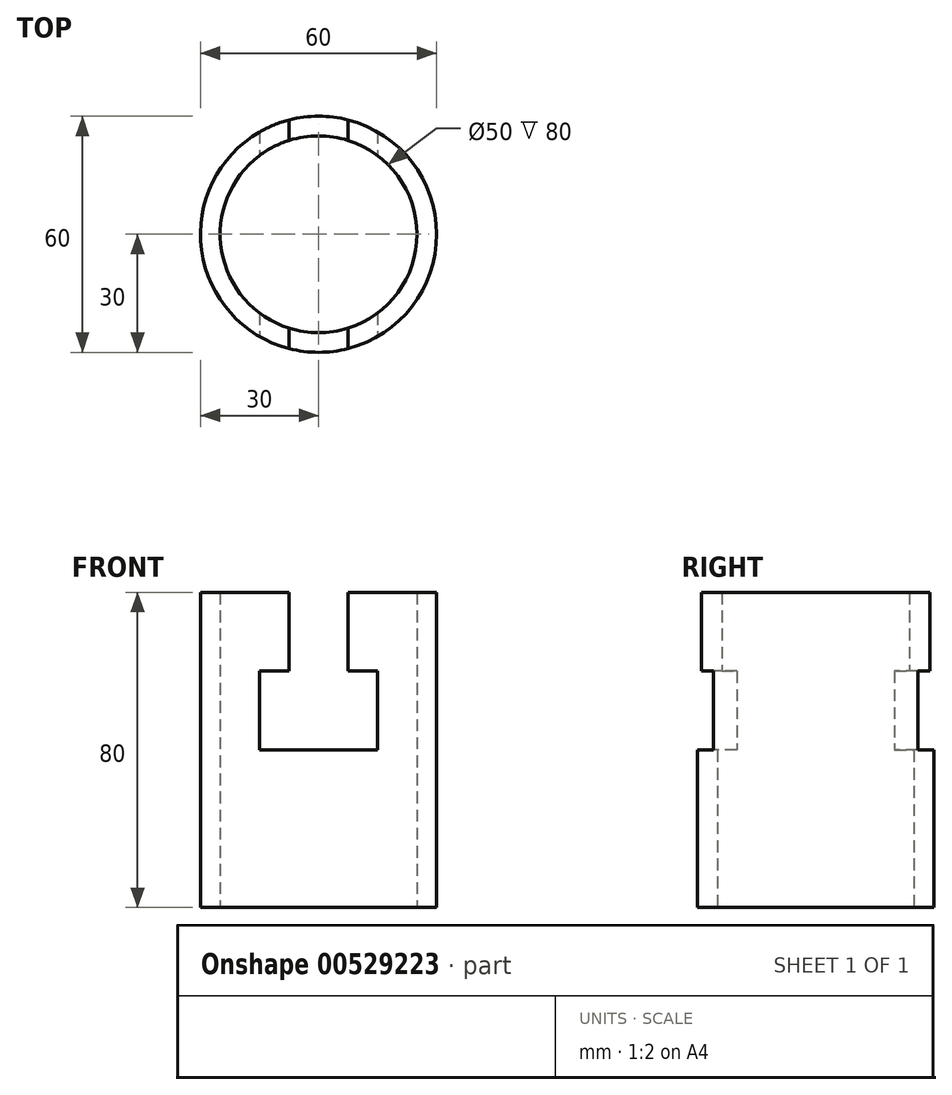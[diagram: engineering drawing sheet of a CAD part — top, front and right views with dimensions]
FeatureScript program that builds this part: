
annotation { "Feature Type Name" : "Feature", "Feature Type Description" : "" }
export const myFeature = defineFeature(function(context is Context, id is Id, definition is map)
    precondition{}
    {
        {
            var Q0;
            Q0=qCreatedBy(makeId("Top.planeOp"),FACE);
            var sketch = newSketch(context, id + "F0", { "sketchPlane" : qUnion([Q0])});
            skCircle(sketch, "E0", {"center": v(0, 0) * mm, "radius": 30 * mm});
            skCircle(sketch, "E1", {"center": v(0, 0) * mm, "radius": 25 * mm});
            skSolve(sketch);
        }
        {
            var Q0;
            Q0=makeQuery(id+"F0.imprint","IMPRINT",FACE,{"disambiguationData":[TD([[makeQuery(id+"F0.imprint","IMPRINT",EDGE,{"derivedFrom":sQuery(id+"F0.wireOp",EDGE,"E0")}),1.0]])]});
            extrude(context, id + "F1", {"entities" : qUnion([Q0]), "endBound" : BoundingType.SYMMETRIC, "depth" : 80 * mm, "offsetDistance" : 25 * mm});
        }
        {
            var Q0;
            Q0=qCreatedBy(makeId("Front.planeOp"),FACE);
            var sketch = newSketch(context, id + "F2", { "sketchPlane" : qUnion([Q0])});
            skLineSegment(sketch, "E2.0", {"start": v(-30, 40) * mm, "end": v(30, 40) * mm, "construction": true});
            skLineSegment(sketch, "E3", {"start": v(0, 40) * mm, "end": v(0, 0) * mm, "construction": true});
            skLineSegment(sketch, "E4", {"start": v(-7.5, 40) * mm, "end": v(-7.5, 20) * mm});
            skLineSegment(sketch, "E5", {"start": v(-7.5, 20) * mm, "end": v(-15, 20) * mm});
            skLineSegment(sketch, "E6", {"start": v(-15, 20) * mm, "end": v(-15, 0) * mm});
            skLineSegment(sketch, "E7", {"start": v(-15, 0) * mm, "end": v(15, 0) * mm});
            skLineSegment(sketch, "E8", {"start": v(15, 0) * mm, "end": v(15, 20) * mm});
            skLineSegment(sketch, "E9", {"start": v(15, 20) * mm, "end": v(7.5, 20) * mm});
            skLineSegment(sketch, "E10", {"start": v(7.5, 20) * mm, "end": v(7.5, 40) * mm});
            skLineSegment(sketch, "E11", {"start": v(7.5, 40) * mm, "end": v(-7.5, 40) * mm});
            skSolve(sketch);
        }
        {
            var Q0;
            Q0 = qSketchRegion(id + "F2", true);
            extrude(context, id + "F3", {"entities" : qUnion([Q0]), "operationType" : NewBodyOperationType.REMOVE, "endBound" : BoundingType.SYMMETRIC, "oppositeDirection" : true, "depth" : 105.6 * mm, "offsetDistance" : 25 * mm});
        }
    });
